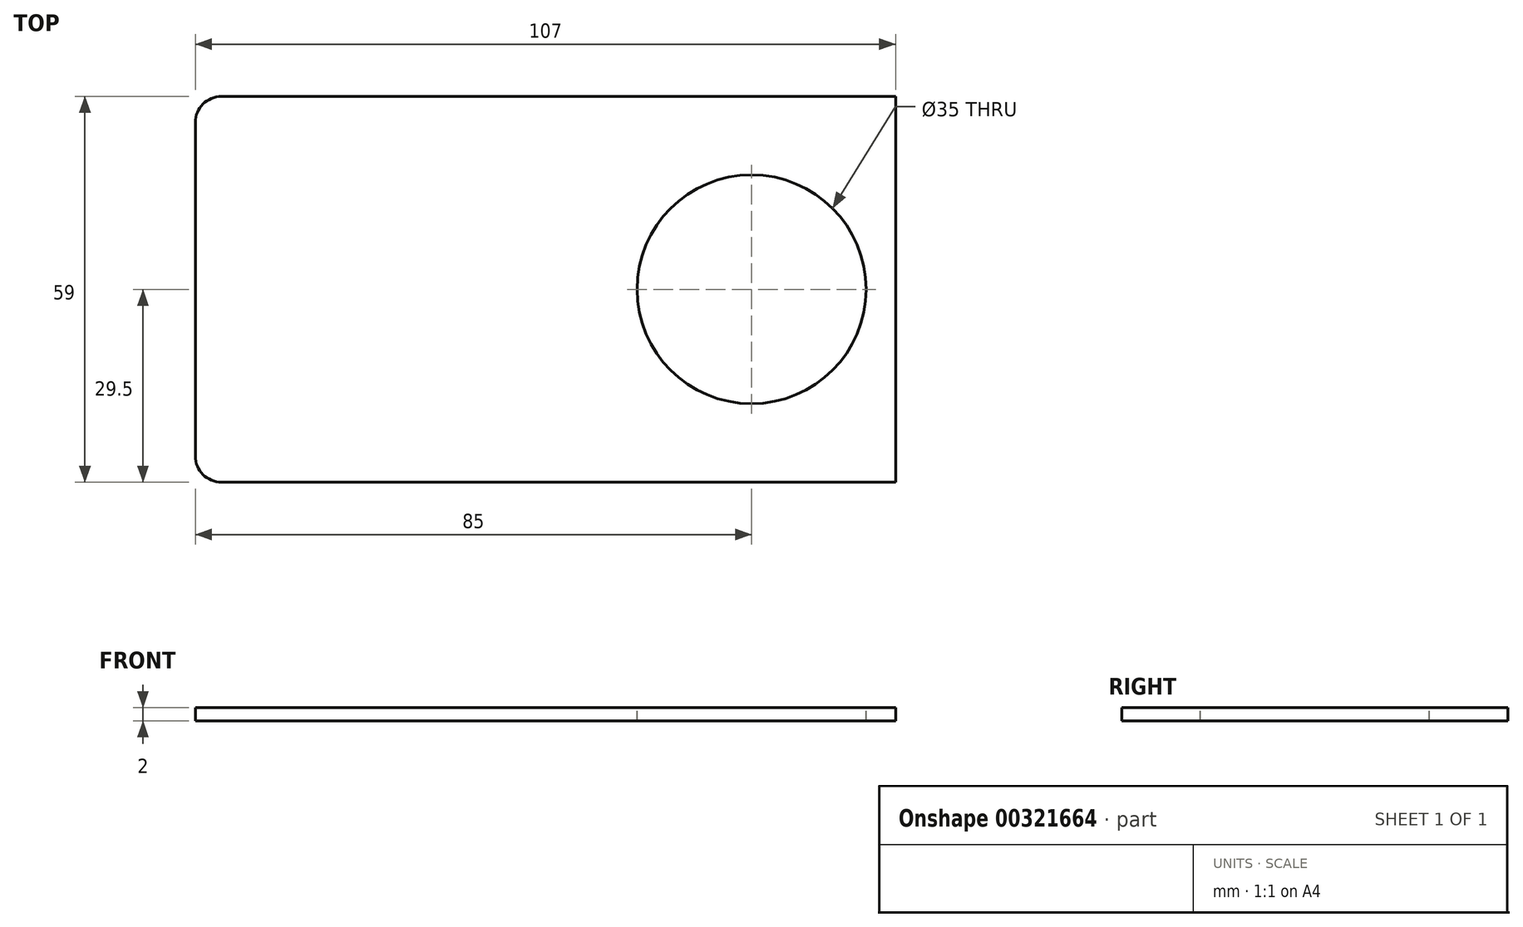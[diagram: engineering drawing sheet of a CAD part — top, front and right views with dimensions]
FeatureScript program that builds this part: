
annotation { "Feature Type Name" : "Feature", "Feature Type Description" : "" }
export const myFeature = defineFeature(function(context is Context, id is Id, definition is map)
    precondition{}
    {
        {
            var Q0;
            Q0=qCreatedBy(makeId("Top.planeOp"),FACE);
            var sketch = newSketch(context, id + "F0", { "sketchPlane" : qUnion([Q0])});
            skLineSegment(sketch, "E0.bottom", {"start": v(43.5, 29.5) * mm, "end": v(-43.5, 29.5) * mm});
            skLineSegment(sketch, "E0.top", {"start": v(43.5, -29.5) * mm, "end": v(-43.5, -29.5) * mm});
            skLineSegment(sketch, "E0.left", {"start": v(43.5, 29.5) * mm, "end": v(43.5, -29.5) * mm});
            skLineSegment(sketch, "E0.right", {"start": v(-43.5, 29.5) * mm, "end": v(-43.5, -29.5) * mm});
            skPoint(sketch, "E0.middle", {"position": v(0, 0) * mm});
            skSolve(sketch);
        }
        {
            var Q0;
            Q0=makeQuery(id+"F0.imprint","IMPRINT",FACE,{"disambiguationData":[TD([[makeQuery(id+"F0.imprint","IMPRINT",EDGE,{"derivedFrom":sQuery(id+"F0.wireOp",EDGE,"E0.bottom")}),1.0]])]});
            extrude(context, id + "F1", {"entities" : qUnion([Q0]), "depth" : 2 * mm});
        }
        {
            var Q0;
            Q0=makeQuery(id+"F1.opExtrude","CAP_FACE",FACE,{"disambiguationData":[OSD([sQuery(id+"F0.wireOp",EDGE,"E0.bottom"),sQuery(id+"F0.wireOp",EDGE,"E0.top"),sQuery(id+"F0.wireOp",EDGE,"E0.left"),sQuery(id+"F0.wireOp",EDGE,"E0.right")])],"isStart":false});
            var sketch = newSketch(context, id + "F2", { "sketchPlane" : qUnion([Q0])});
            skCircle(sketch, "E1", {"center": v(21.5, 0) * mm, "radius": 17.5 * mm});
            skSolve(sketch);
        }
        {
            var Q0;
            Q0=makeQuery(id+"F2.imprint","IMPRINT",FACE,{"disambiguationData":[TD([[makeQuery(id+"F2.imprint","IMPRINT",EDGE,{"derivedFrom":sQuery(id+"F2.wireOp",EDGE,"E1")}),1.0]])]});
            extrude(context, id + "F3", {"entities" : qUnion([Q0]), "operationType" : NewBodyOperationType.REMOVE, "oppositeDirection" : true, "depth" : 25 * mm});
        }
        {
            var Q0;
            Q0=makeQuery(id+"F1.opExtrude","SWEPT_FACE",FACE,{"disambiguationData":[OSD([sQuery(id+"F0.wireOp",EDGE,"E0.right")])]});
            extrude(context, id + "F4", {"entities" : qUnion([Q0]), "operationType" : NewBodyOperationType.ADD, "depth" : 20 * mm});
        }
        {
            var Q0;
            Q0=makeQuery(id+"F4.opExtrude","CAP_EDGE",EDGE,{"disambiguationData":[OSD([sQuery(id+"F0.wireOp",EDGE,"E0.bottom"),sQuery(id+"F0.wireOp",EDGE,"E0.right")])],"isStart":false});
            var Q1;
            Q1=makeQuery(id+"F4.opExtrude","CAP_EDGE",EDGE,{"disambiguationData":[OSD([sQuery(id+"F0.wireOp",EDGE,"E0.top"),sQuery(id+"F0.wireOp",EDGE,"E0.right")])],"isStart":false});
            fillet(context, id + "F5", {"entities" : qUnion([Q0, Q1]), "radius" : 4 * mm, "tangentPropagation" : true, "allowEdgeOverflow" : false});
        }
    });
